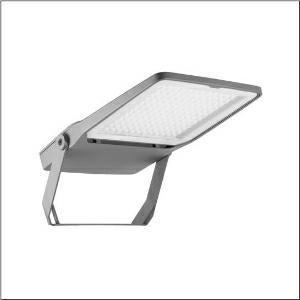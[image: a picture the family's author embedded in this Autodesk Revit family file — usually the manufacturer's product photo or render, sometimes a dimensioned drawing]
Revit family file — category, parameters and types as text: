
# Revit family: floodlight_fl_20_midi___pl52_5xa7682d1d1ac_0cf7
name_source: partatom
category: Lighting Fixtures
units: mm (PartAtom-declared; Revit-internal decimal feet)

## family parameters
Cut with Voids When Loaded = No
Host = Face
Light Source = No
Part Type = Normal
Room Calculation Point = No
Round Connector Dimension = Use Diameter
Shared = No

## types (1)
- --- (1 x LED 3000K / CRI = 80 (unbekannt), 14130 lm, 3000K)
    Apparent Load = 142 VA
    CIE Flux Codes = 27 59 98 100 100
    Color Rendering = 80
    Color Temperature = 3000K
    Default Elevation = 1800 mm
    Description = Floodlight FL 20 midi, floodlight, primary light control with lens, of plastic, primary optical cover: protective disc, of toughened safety glass, transparent, light distribution: PL52, light emission: direct distribution, primary light characteristic: asymmetric, installation type: surface-mounted, LED High Power LED, rated luminous flux: 14.130 lm, light colour: 830, colour temperature: 3000K, control gear: ECG Plus, control: flexible luminous flux parameterisation, time-dependent luminous flux control, digital communication interface, power reduction, overheat protection, electronic power reduction, with terminal, 5-pole, max. 2.5mm², mains connection: 220..240V, AC, 50/60Hz, rated input power: 142W, LED unit, of diecast aluminium, powder-coated, Siteco® metallic grey (DB 702S), length: 654 mm, width: 450 mm, height: 76mm, housing frame, of diecast aluminium, powder-coated, Siteco® metallic grey (DB 702S), mounting bracket, of steel, powder-coated, Siteco® metallic grey (DB 702S), DALIprotection rating (complete): IP66, insulation class (complete): insulation class II (safety insulation), certification: CE, ENEC, VDE, protection symbol: D, permissible ambient temperature for indoor applications: -40..+40°C, permissible ambient temperature for outdoor applications: -40..+50°C, standard: DIN EN 12944, packaging unit: 1 piece

Light Distribution: PL52
    Height = 76 mm
    Lamp = 1 x LED 3000K / CRI >= 80 (unbekannt)
    Lamp Light Flux = 14130 lm
    Lamp count = 1
    Length = 672 mm
    Luminous efficacy = 100 lm/W
    Manufacturer = Siteco
    ModVariant = No
    Model = 5XA7682D1D1AC
    Number of Poles = 1
    OnlyDefault = Yes
    Power Factor = 1
    Product Name = Floodlight FL 20 midi | PL52
    Product group = floodlight | pylon top
    ProductGroupID = 6101
    Protection Class = Protection class II
    Protection Degree = IP 66
    RLX_Detail_Level = 1
    RlxData = <blob elided: 97881 chars, md5=03911e74>
    Socket = socket
    Standby Power = 0 W
    System Light Flux = 14130 lm
    System Power = 142 W
    Type Comments = factory setting: luminous flux: 100 % | dim-lin: 254 | 489 mA
    Type Image = l_1005943.jpg
    URL = http://relux.com
    VarID = @adj_143405
    Voltage = 0 V
    Weight = 0.00 kg
    Width = 450 mm

## geometry (parser evidence)
native form markers: Blend x4, Sweep x12
no freeform markers — native parametric forms only
